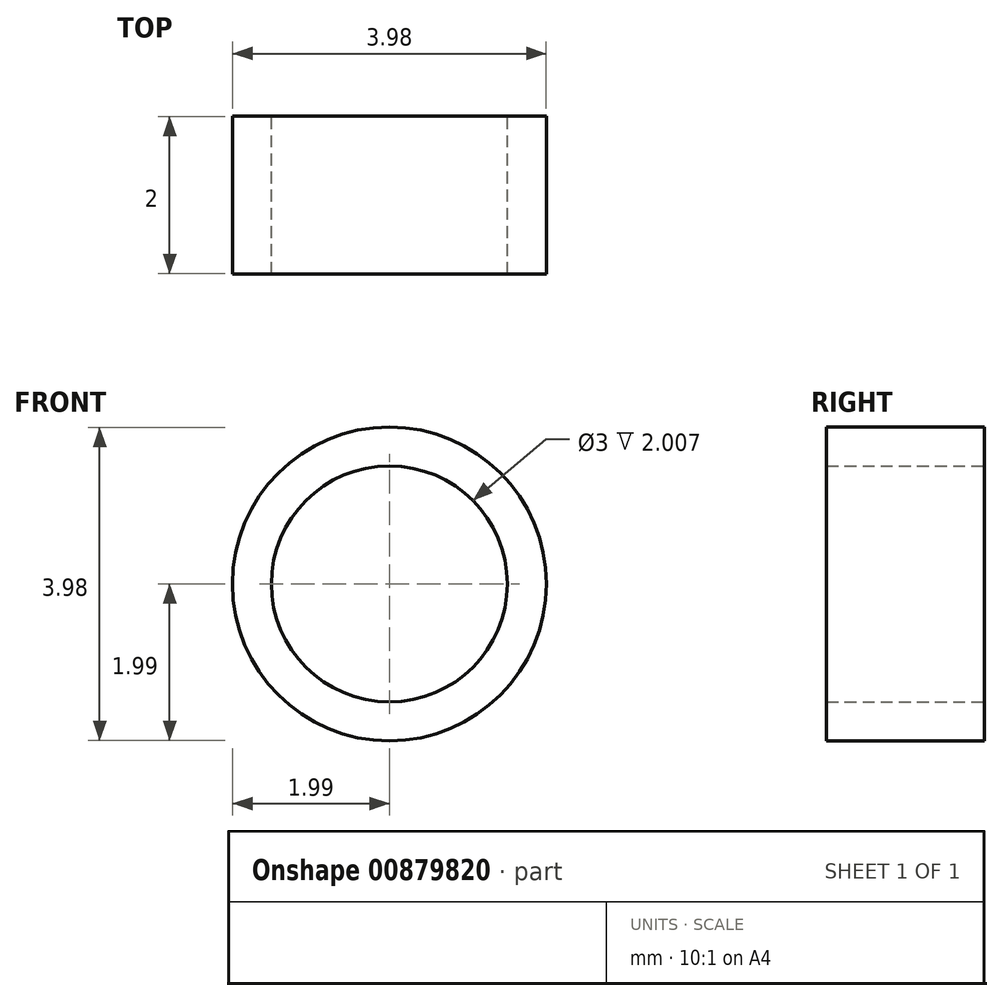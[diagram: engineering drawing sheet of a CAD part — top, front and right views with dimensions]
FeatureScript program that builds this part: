
annotation { "Feature Type Name" : "Feature", "Feature Type Description" : "" }
export const myFeature = defineFeature(function(context is Context, id is Id, definition is map)
    precondition{}
    {
        {
            var Q0;
            Q0=qCreatedBy(makeId("Front.planeOp"),FACE);
            var sketch = newSketch(context, id + "F0", { "sketchPlane" : qUnion([Q0])});
            skCircle(sketch, "E0", {"center": v(0, 0) * mm, "radius": 1.5 * mm});
            skCircle(sketch, "E1", {"center": v(0, 0) * mm, "radius": 2 * mm});
            skSolve(sketch);
        }
        {
            var Q0;
            Q0=makeQuery(id+"F0.imprint","IMPRINT",FACE,{"disambiguationData":[TD([[makeQuery(id+"F0.imprint","IMPRINT",EDGE,{"derivedFrom":sQuery(id+"F0.wireOp",EDGE,"E0")}),-1.0]])]});
            extrude(context, id + "F1", {"entities" : qUnion([Q0]), "endBound" : BoundingType.SYMMETRIC, "depth" : 2 * mm, "offsetDistance" : 25.4 * mm});
        }
    });
